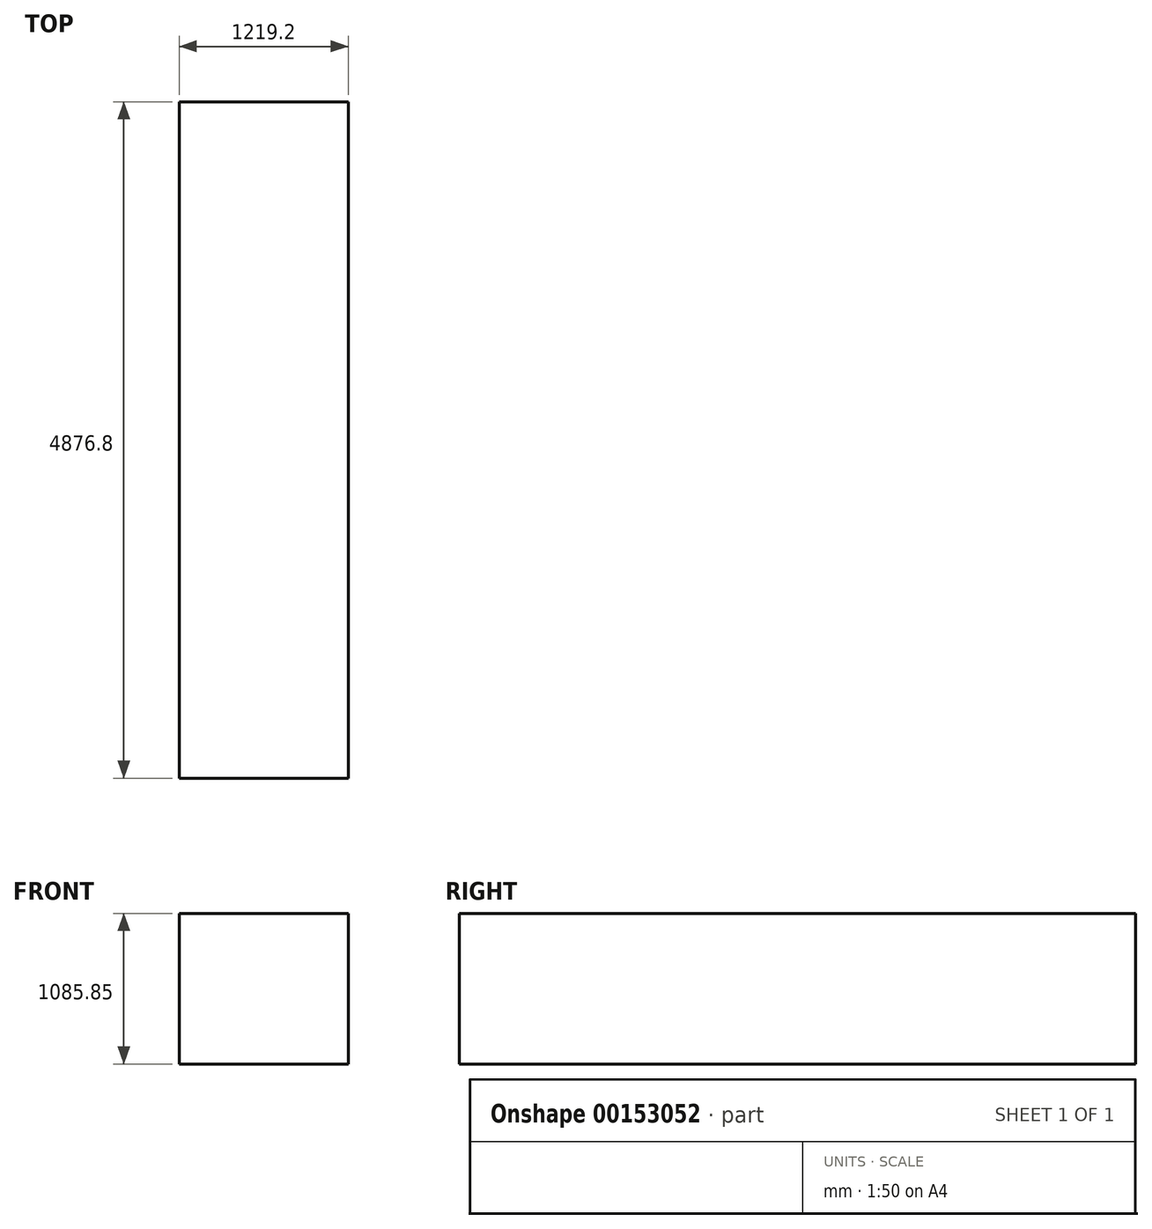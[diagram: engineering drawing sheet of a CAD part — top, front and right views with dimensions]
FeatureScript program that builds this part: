
annotation { "Feature Type Name" : "Feature", "Feature Type Description" : "" }
export const myFeature = defineFeature(function(context is Context, id is Id, definition is map)
    precondition{}
    {
        {
            var Q0;
            Q0=qCreatedBy(makeId("Top.planeOp"),FACE);
            var sketch = newSketch(context, id + "F0", { "sketchPlane" : qUnion([Q0])});
            skLineSegment(sketch, "E0.bottom", {"start": v(0, 0) * mm, "end": v(-1219.2, 0) * mm});
            skLineSegment(sketch, "E0.top", {"start": v(0, -4876.8) * mm, "end": v(-1219.2, -4876.8) * mm});
            skLineSegment(sketch, "E0.left", {"start": v(0, 0) * mm, "end": v(0, -4876.8) * mm});
            skLineSegment(sketch, "E0.right", {"start": v(-1219.2, 0) * mm, "end": v(-1219.2, -4876.8) * mm});
            skSolve(sketch);
        }
        {
            var Q0;
            Q0 = qSketchRegion(id + "F0", true);
            extrude(context, id + "F1", {"entities" : qUnion([Q0]), "depth" : 1085.85 * mm});
        }
    });
